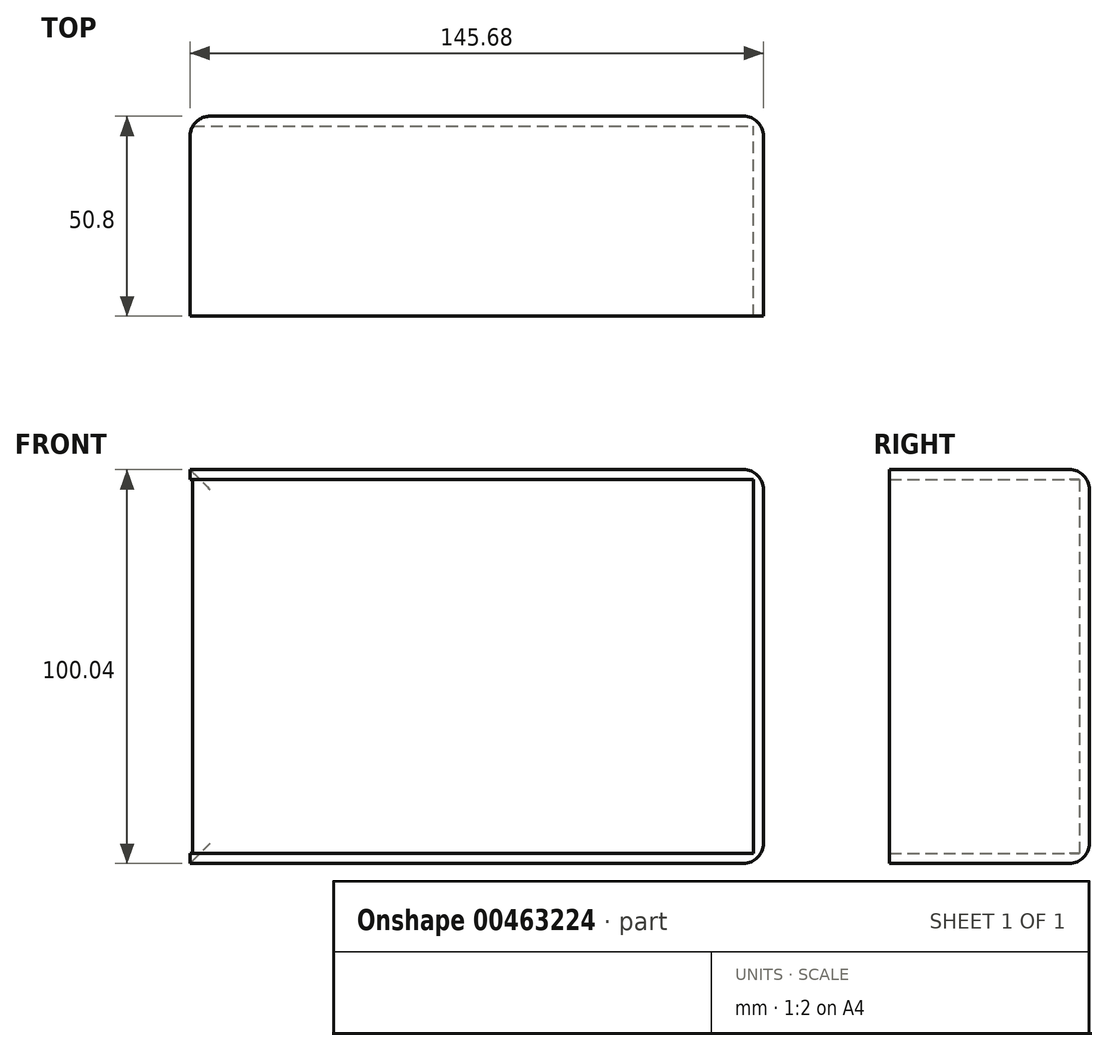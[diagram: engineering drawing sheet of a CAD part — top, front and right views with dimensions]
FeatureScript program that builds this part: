
annotation { "Feature Type Name" : "Feature", "Feature Type Description" : "" }
export const myFeature = defineFeature(function(context is Context, id is Id, definition is map)
    precondition{}
    {
        {
            var Q0;
            Q0=qCreatedBy(makeId("Front.planeOp"),FACE);
            var sketch = newSketch(context, id + "F0", { "sketchPlane" : qUnion([Q0])});
            skLineSegment(sketch, "E0.bottom", {"start": v(-93, 52.95) * mm, "end": v(52.68, 52.95) * mm});
            skLineSegment(sketch, "E0.top", {"start": v(-93, -47.09) * mm, "end": v(52.68, -47.09) * mm});
            skLineSegment(sketch, "E0.left", {"start": v(-93, 52.95) * mm, "end": v(-93, -47.09) * mm});
            skLineSegment(sketch, "E0.right", {"start": v(52.68, 52.95) * mm, "end": v(52.68, -47.09) * mm});
            skLineSegment(sketch, "E1.bottom", {"start": v(-90.11, -43.43) * mm, "end": v(48.7, -43.43) * mm});
            skLineSegment(sketch, "E1.top", {"start": v(-90.11, 49.5) * mm, "end": v(48.7, 49.5) * mm});
            skLineSegment(sketch, "E1.left", {"start": v(-90.11, -43.43) * mm, "end": v(-90.11, 49.5) * mm});
            skLineSegment(sketch, "E1.right", {"start": v(48.7, -43.43) * mm, "end": v(48.7, 49.5) * mm});
            skSolve(sketch);
        }
        {
            var Q0;
            Q0 = qSketchRegion(id + "F0", true);
            var Q1;
            Q1=makeQuery(id+"F0.imprint","IMPRINT",FACE,{"disambiguationData":[TD([[makeQuery(id+"F0.imprint","IMPRINT",EDGE,{"derivedFrom":sQuery(id+"F0.wireOp",EDGE,"E1.bottom")}),1.0]])]});
            extrude(context, id + "F1", {"entities" : qUnion([Q0, Q1]), "depth" : 25.4 * mm});
        }
        {
            var Q0;
            Q0=makeQuery(id+"F1.opExtrude","CAP_FACE",FACE,{"disambiguationData":[OSD([sQuery(id+"F0.wireOp",EDGE,"E0.bottom"),sQuery(id+"F0.wireOp",EDGE,"E0.top"),sQuery(id+"F0.wireOp",EDGE,"E0.left"),sQuery(id+"F0.wireOp",EDGE,"E0.right")])],"isStart":false});
            var Q1;
            Q1=makeQuery(id+"F1.opExtrude","SWEPT_FACE",FACE,{"disambiguationData":[OSD([sQuery(id+"F0.wireOp",EDGE,"E0.left")])]});
            shell(context, id + "F2", {"entities" : qUnion([Q0, Q1]), "thickness" : 2.54 * mm});
        }
        {
            var Q0;
            Q0=makeQuery(id+"F1.opExtrude","CAP_FACE",FACE,{"disambiguationData":[OSD([sQuery(id+"F0.wireOp",EDGE,"E0.bottom"),sQuery(id+"F0.wireOp",EDGE,"E0.top"),sQuery(id+"F0.wireOp",EDGE,"E0.left"),sQuery(id+"F0.wireOp",EDGE,"E0.right")])],"isStart":true});
            fillet(context, id + "F3", {"entities" : qUnion([Q0]), "radius" : 5.08 * mm, "tangentPropagation" : true, "allowEdgeOverflow" : false});
        }
        {
            var Q0;
            Q0=makeQuery(id+"F1.opExtrude","CAP_FACE",FACE,{"disambiguationData":[OSD([sQuery(id+"F0.wireOp",EDGE,"E0.bottom"),sQuery(id+"F0.wireOp",EDGE,"E0.top"),sQuery(id+"F0.wireOp",EDGE,"E0.left"),sQuery(id+"F0.wireOp",EDGE,"E0.right")])],"isStart":false});
            extrude(context, id + "F4", {"entities" : qUnion([Q0]), "operationType" : NewBodyOperationType.ADD, "depth" : 25.4 * mm});
        }
        {
            var Q0;
            {var subQ0=sQuery(id+"F0.wireOp",EDGE,"E0.right");var subQ1=sQuery(id+"F0.wireOp",EDGE,"E0.bottom");Q0=makeQuery(id+"F4.boolean.opBoolean","MERGE",EDGE,{"derivedFrom":[makeQuery(id+"F1.opExtrude","SWEPT_EDGE",EDGE,{"disambiguationData":[OSD([subQ1,subQ0])]}),makeQuery(id+"F4.opExtrude","SWEPT_EDGE",EDGE,{"disambiguationData":[OSD([subQ1,subQ0]),TDD([makeQuery(id+"F1.opExtrude","CAP_VERTEX",VERTEX,{"disambiguationData":[OSD([subQ1,subQ0])],"isStart":false})])]})]});}
            var Q1;
            {var subQ0=sQuery(id+"F0.wireOp",EDGE,"E0.right");var subQ1=sQuery(id+"F0.wireOp",EDGE,"E0.top");Q1=makeQuery(id+"F4.boolean.opBoolean","MERGE",EDGE,{"derivedFrom":[makeQuery(id+"F1.opExtrude","SWEPT_EDGE",EDGE,{"disambiguationData":[OSD([subQ1,subQ0])]}),makeQuery(id+"F4.opExtrude","SWEPT_EDGE",EDGE,{"disambiguationData":[OSD([subQ1,subQ0]),TDD([makeQuery(id+"F1.opExtrude","CAP_VERTEX",VERTEX,{"disambiguationData":[OSD([subQ1,subQ0])],"isStart":false})])]})]});}
            fillet(context, id + "F5", {"entities" : qUnion([Q0, Q1]), "radius" : 5.08 * mm, "tangentPropagation" : true, "allowEdgeOverflow" : false});
        }
    });
